# Revit family: ToiletPaperDispenser_Metlam_Dual
name_source: partatom
category: Generic Models
revit_build: Autodesk Revit Architecture 2013 (Build: 20120221_2030(x64)
units: mm (PartAtom-declared; Revit-internal decimal feet)

## types (2) — shared parameters
Assembly Code = E1090900
Default Elevation = 1219 mm
Depth = 126 mm  [stored 0.413386 ft]
Description = Dual Toilet Paper Dispenser
FilterObject_ANZRS = Toilet Paper Dispenser
Height = 310 mm  [stored 1.01706 ft]
Keywords = CAPACITY 2 Rolls standard core toilet tissue one above the other
Manufacturer = Metlam
ModifiedIssue_ANZRS = 130318.01 $
StyleOrType_ANZRS = Sanitary Ware
URL = http://www.metlam.com.au
Width = 118 mm

## per-type parameters (varying)
| type | Material Main | Model | Product Code |
| Metlam Dual TPD - Stainless Steel | Stainless Steel, Satin | Dual Surface Mounted - Stainless Steel | ML 832 SS |
| Metlam Dual TPD - White Powder Coat | Stainless Steel, White Powder Coat | Dual Surface Mounted - White Powder Coat | ML 832 W |

note: [stored X ft] marks values corroborated as IEEE doubles in the binary element streams (Revit-internal decimal feet)

## geometry (parser evidence)
native form markers: Blend x11, Sweep x1
no freeform markers — native parametric forms only
